# Revit family: R 301 Ultra (a)
name_source: partatom
category: Equipement spécialisé
revit_build: Autodesk Revit LT 2015 (Build: 20140606_1530(x64)
units: mm (PartAtom-declared; Revit-internal decimal feet)

## types (5) — shared parameters
Apparent Power = 0 VA
Depth Coupe-Légumes = 306 mm
Depth Cutter = 305 mm
Depth Electrique connexion = 40 mm  [stored 0.131234 ft]
Description = COMBINES
Fabricant = ROBOT COUPE
Height Coupe-Légumes = 565 mm
Height Cutter = 425 mm
Modèle = R 301 Ultra
Phase = 1
UP Depth Coupe-Légumes = 376 mm  [stored 1.2336 ft]
UP Height Coupe-Légumes = 660 mm
UP Width Coupe-Légumes = 488 mm
URL = www.robot-coupe.com
Width Coupe-Légumes = 417 mm
Width Cutter = 225 mm
water = Connector
zero-valued in all types: Cold water supply, Cold water supply height, Used water, Waste water height

## per-type parameters (varying)
| type | Amps | Cycle | HP | Speeds (Rpm) | Volts | Watts | Weight |
| R 301 Ultra  230/50/1 | 5.7 A | 50 Hz |  | 1500 | 230 V | 650 W | 17 kg |
| R 301 Ultra  120/60/1 | 12 A | 60 Hz |  | 1500 | 120 V | 650 W | 17 kg |
| R 301 Ultra  220/60/1 | 5.7 A | 60 Hz |  | 1500 | 220 V | 650 W | 17 kg |
| R 301 Ultra  220-240/50/1 | 5.7 A | 50 Hz |  | 1500 | 220 V | 650 W | 17 kg |
| R 301 Ultra  USA  120/60/1 | 12 A | 60 Hz | 1.5 | 1725 | 120 V | 0 W | 36 lbs |

note: [stored X ft] marks values corroborated as IEEE doubles in the binary element streams (Revit-internal decimal feet)

## geometry (parser evidence)
native form markers: Blend x77, Sweep x5
no freeform markers — native parametric forms only
